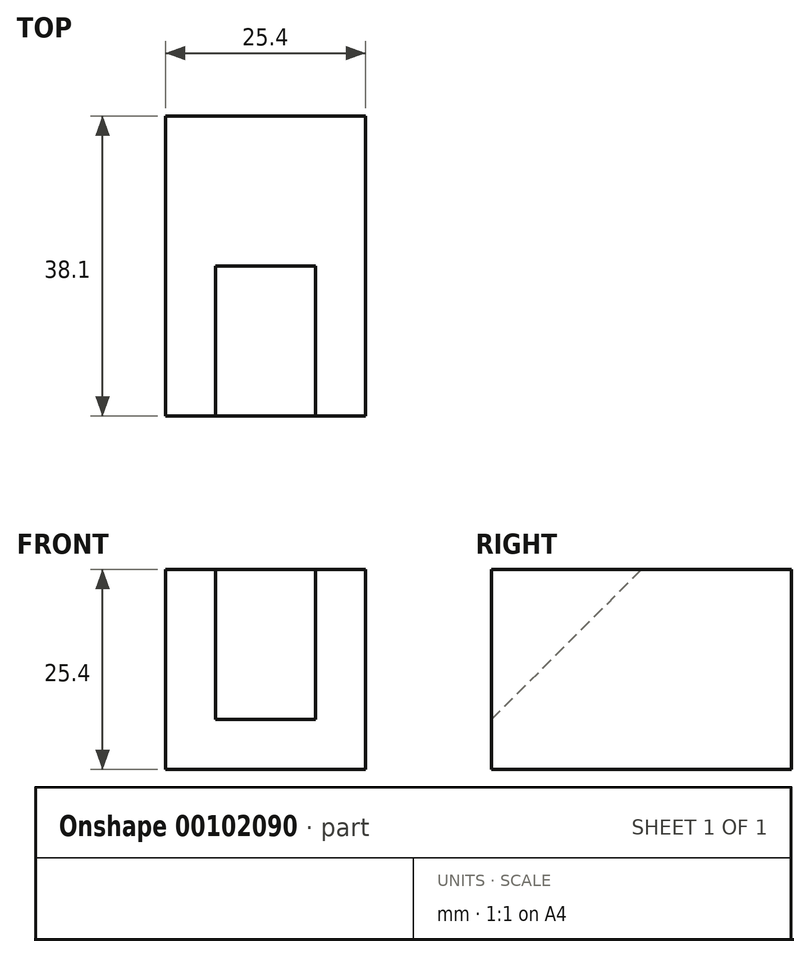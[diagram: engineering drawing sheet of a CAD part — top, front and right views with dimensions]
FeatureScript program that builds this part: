
annotation { "Feature Type Name" : "Feature", "Feature Type Description" : "" }
export const myFeature = defineFeature(function(context is Context, id is Id, definition is map)
    precondition{}
    {
        {
            var Q0;
            Q0=qCreatedBy(makeId("Right.planeOp"),FACE);
            var sketch = newSketch(context, id + "F0", { "sketchPlane" : qUnion([Q0])});
            skLineSegment(sketch, "E0", {"start": v(0, 0) * mm, "end": v(0, 25.4) * mm});
            skLineSegment(sketch, "E1", {"start": v(0, 25.4) * mm, "end": v(38.1, 25.4) * mm});
            skLineSegment(sketch, "E2", {"start": v(38.1, 25.4) * mm, "end": v(38.1, 0) * mm});
            skLineSegment(sketch, "E3", {"start": v(38.1, 0) * mm, "end": v(0, 0) * mm});
            skSolve(sketch);
        }
        {
            var Q0;
            Q0 = qSketchRegion(id + "F0", true);
            extrude(context, id + "F1", {"entities" : qUnion([Q0]), "endBound" : BoundingType.SYMMETRIC, "depth" : 25.4 * mm});
        }
        {
            var Q0;
            Q0=makeQuery(id+"F1.opExtrude","CAP_FACE",FACE,{"disambiguationData":[OSD([sQuery(id+"F0.wireOp",EDGE,"E0"),sQuery(id+"F0.wireOp",EDGE,"E1"),sQuery(id+"F0.wireOp",EDGE,"E2"),sQuery(id+"F0.wireOp",EDGE,"E3")])],"isStart":false});
            var sketch = newSketch(context, id + "F2", { "sketchPlane" : qUnion([Q0])});
            skLineSegment(sketch, "E4", {"start": v(0, 6.35) * mm, "end": v(19.05, 25.4) * mm});
            skLineSegment(sketch, "E5", {"start": v(19.05, 25.4) * mm, "end": v(0, 25.4) * mm});
            skLineSegment(sketch, "E6", {"start": v(0, 25.4) * mm, "end": v(0, 6.35) * mm});
            skSolve(sketch);
        }
        {
            var Q0;
            Q0 = qSketchRegion(id + "F2", true);
            extrude(context, id + "F3", {"entities" : qUnion([Q0]), "operationType" : NewBodyOperationType.REMOVE, "oppositeDirection" : true, "depth" : 19.05 * mm, "hasSecondDirection" : true, "secondDirectionOppositeDirection" : true, "secondDirectionDepth" : 6.35 * mm});
        }
    });
